# Revit family: Armario Linkeo DC anchura 800
name_source: partatom
category: Equipement spécialisé
units: mm (PartAtom-declared; Revit-internal decimal feet)

## family parameters
Basée sur le plan de construction = Non
Cote de connecteur circulaire = Utiliser le diamètre
Couper avec des vides une fois chargée = Non
Partagée = Oui
Point de calcul de pièce = Non
Toujours verticalement = Oui
Type d'élément = Normal

## types (4) — shared parameters
Altura útil (mm) = 1881 mm  [stored 6.17126 ft]
Anchura (mm) = 800 mm  [stored 2.62467 ft]
Clase de aplicación = EC002499
Clase de protección IK = IK02
Clase de protección IP = IP20
Color = IDS_NOIR
Con conexión a tierra = Oui
Con puerta frontal = Oui
Con techo en chapa = Oui
Distancia de la apertura 1 = 275 mm
E-catalogo enlace = https://www.legrand.fr
Función = Servidores  Linkeo DC
Material = Acero
Material de la puerta frontal = IDS_ACIER
Modelo = Estructura fija
Modelo de anchura = 800 mm  [stored 2.62467 ft]
Máxima capacidad de carga = 1500
Numero RAL = 9005
Número de puertas = 1
Sistema de cierre de la puerta frontal = Con tres puntos
Tamaño modular = 19 pulgadas
Temperatura de almacenamiento = -25°C à 70°C
Temperatura operativa = -25°C à 70°C
Tipo de montaje = Antes y atrás
Tipo de ventilación = Passiva
Tratamiento de superficie = Recubrimiento con polvo
Ubicación del rack = 93 mm  [stored 0.305118 ft]
zero-valued in all types: Elévation par défaut

## per-type parameters (varying)
| type | Altura | Altura del modelo | Anchura útil (mm) | Formulación BIM | Módulos de altura | Número de pieza Legrand | Profundidad | Profundidad del modelo (mm) |
| Armario Linkeo2 42U 800x1000 | 2047 mm  [stored 6.71588 ft] | 1965 mm  [stored 6.44685 ft] | 890 mm  [stored 2.91995 ft] | Armario Linkeo2 42U 800x1000 equipado | 42 | 446802 | 1000 mm  [stored 3.28084 ft] | 1000 mm  [stored 3.28084 ft] |
| Armario Linkeo2 42U 800x1200 | 2047 mm  [stored 6.71588 ft] | 1965 mm  [stored 6.44685 ft] | 1090 mm  [stored 3.57612 ft] | Armario Linkeo2 42U 800x1200 equipado | 42 | 446803 | 1200 mm | 1200 mm |
| Armario Linkeo2 47U 800x1000 | 2269 mm | 2190 mm  [stored 7.18504 ft] | 890 mm  [stored 2.91995 ft] | Armario Linkeo2 47U 800x1000 equipado | 47 | 446806 | 1000 mm  [stored 3.28084 ft] | 1000 mm  [stored 3.28084 ft] |
| Armario Linkeo2 47U 800x1200 | 2269 mm | 2190 mm  [stored 7.18504 ft] | 1090 mm  [stored 3.57612 ft] | Armario Linkeo2 47U 800x1200 equipado | 47 | 446807 | 1200 mm | 1200 mm |

note: [stored X ft] marks values corroborated as IEEE doubles in the binary element streams (Revit-internal decimal feet)
